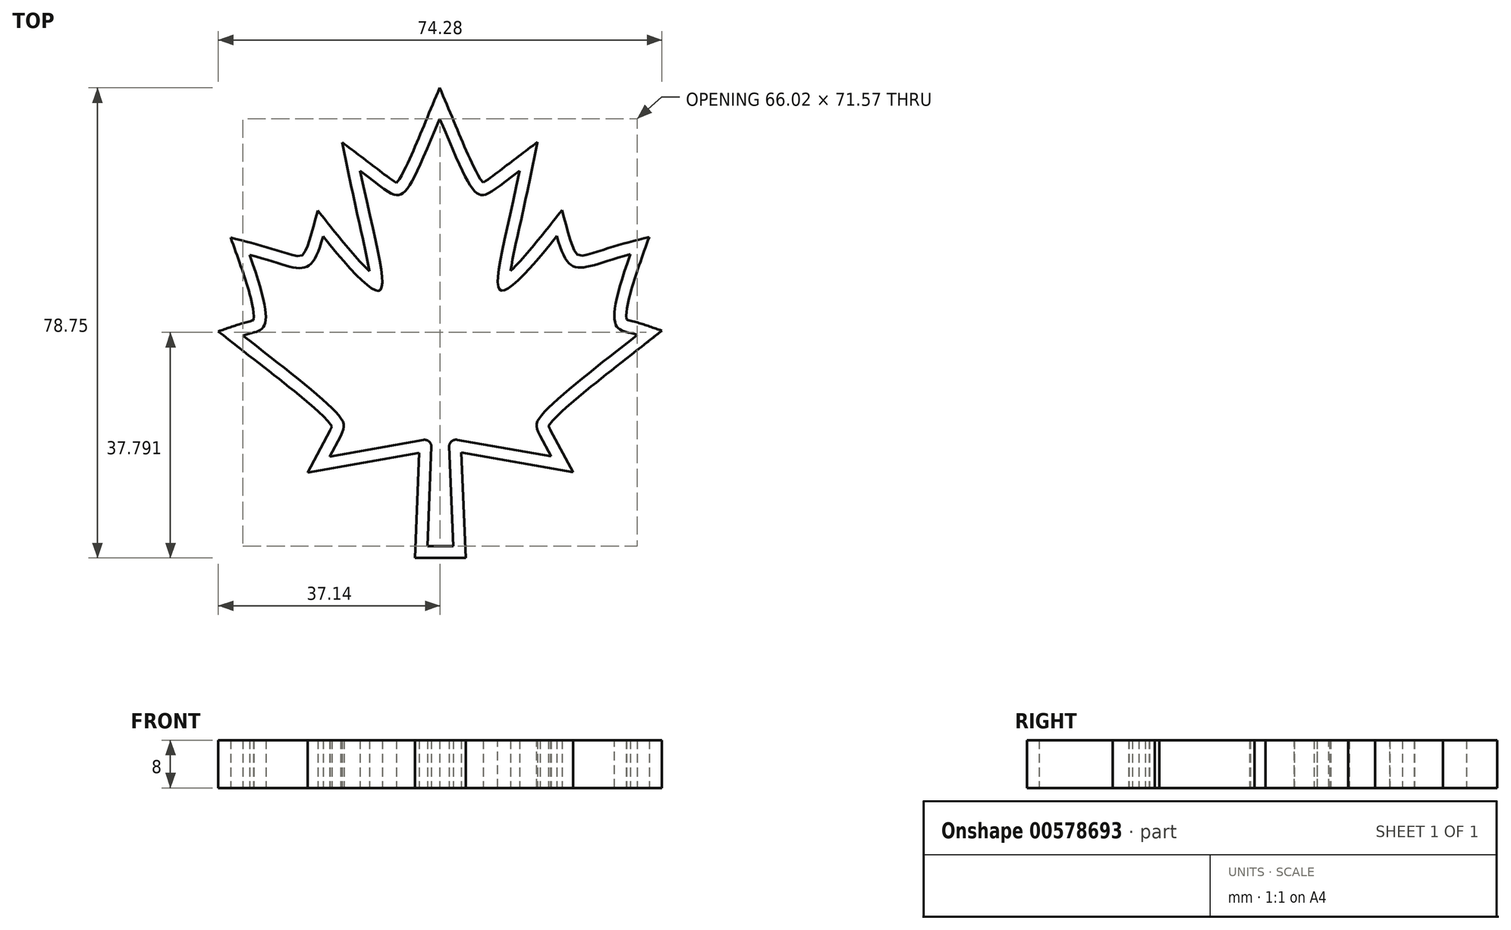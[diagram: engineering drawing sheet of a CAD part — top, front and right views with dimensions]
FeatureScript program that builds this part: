
annotation { "Feature Type Name" : "Feature", "Feature Type Description" : "" }
export const myFeature = defineFeature(function(context is Context, id is Id, definition is map)
    precondition{}
    {
        {
            var Q0;
            Q0=qCreatedBy(makeId("Top.planeOp"),FACE);
            var sketch = newSketch(context, id + "F0", { "sketchPlane" : qUnion([Q0])});
            skLineSegment(sketch, "E0", {"start": v(9.47, -7.07) * mm, "end": v(9.02, 3.36) * mm});
            skLineSegment(sketch, "E1", {"start": v(9.88, 4.04) * mm, "end": v(19.68, 2.32) * mm});
            skLineSegment(sketch, "E2", {"start": v(19.68, 2.32) * mm, "end": v(18.53, 4.47) * mm});
            skFitSpline(sketch, "E3", {"points": [v(18.53, 4.47) * mm, v(18.53, 6.4) * mm, v(28.7, 15.02) * mm], "startDerivative": vector(-4.89, 9.38) * mm, "endDerivative": vector(15.45, 12.25) * mm});
            skArc(sketch, "E4", {"start": v(9.88, 4.04) * mm, "mid": v(9.3, 3.9) * mm, "end": v(9.02, 3.36) * mm});
            skFitSpline(sketch, "E5", {"points": [v(28.7, 15.02) * mm, v(26.74, 15.72) * mm, v(28, 23.47) * mm], "startDerivative": vector(-7.73, 2.6) * mm, "endDerivative": vector(8.14, 22.87) * mm});
            skFitSpline(sketch, "E6", {"points": [v(28, 23.47) * mm, v(20.29, 25.37) * mm], "startDerivative": vector(-15.91, -4.18) * mm, "endDerivative": vector(-4.05, 14.65) * mm});
            skFitSpline(sketch, "E7", {"points": [v(20.29, 25.37) * mm, v(14.46, 19.67) * mm, v(16.38, 32.21) * mm], "startDerivative": vector(-16.61, -21.02) * mm, "endDerivative": vector(7.72, 38.13) * mm});
            skFitSpline(sketch, "E8", {"points": [v(16.38, 32.21) * mm, v(12.19, 29.72) * mm, v(8.04, 37.65) * mm], "startDerivative": vector(-19.33, -14.7) * mm, "endDerivative": vector(-11.74, 27.86) * mm});
            skLineSegment(sketch, "E9", {"start": v(9.47, -7.07) * mm, "end": v(8.11, -7.07) * mm});
            skFitSpline(sketch, "E10.MirrorCS", {"points": [v(-0.3, 32.18) * mm, v(3.91, 29.7) * mm, v(8.04, 37.65) * mm], "startDerivative": vector(19.38, -14.63) * mm, "endDerivative": vector(11.64, 27.9) * mm});
            skFitSpline(sketch, "E11.MirrorCS", {"points": [v(-4.17, 25.33) * mm, v(1.68, 19.65) * mm, v(-0.3, 32.18) * mm], "startDerivative": vector(16.68, -20.97) * mm, "endDerivative": vector(-7.85, 38.1) * mm});
            skFitSpline(sketch, "E12.MirrorCS", {"points": [v(-11.87, 23.4) * mm, v(-4.17, 25.33) * mm], "startDerivative": vector(15.93, -4.13) * mm, "endDerivative": vector(4, 14.66) * mm});
            skFitSpline(sketch, "E13.MirrorCS", {"points": [v(-12.56, 14.95) * mm, v(-10.59, 15.65) * mm, v(-11.87, 23.4) * mm], "startDerivative": vector(7.72, 2.63) * mm, "endDerivative": vector(-8.22, 22.84) * mm});
            skFitSpline(sketch, "E14.MirrorCS", {"points": [v(-2.35, 4.43) * mm, v(-2.35, 6.36) * mm, v(-12.56, 14.95) * mm], "startDerivative": vector(4.86, 9.4) * mm, "endDerivative": vector(-15.49, 12.2) * mm});
            skLineSegment(sketch, "E15.MirrorCS", {"start": v(-3.49, 2.28) * mm, "end": v(-2.35, 4.43) * mm});
            skLineSegment(sketch, "E16.MirrorCS", {"start": v(6.3, 4.03) * mm, "end": v(-3.49, 2.28) * mm});
            skArc(sketch, "E17.MirrorCS", {"start": v(6.3, 4.03) * mm, "mid": v(6.89, 3.89) * mm, "end": v(7.17, 3.36) * mm});
            skLineSegment(sketch, "E18.MirrorCS", {"start": v(6.75, -7.08) * mm, "end": v(7.17, 3.36) * mm});
            skLineSegment(sketch, "E19.MirrorCS", {"start": v(6.75, -7.08) * mm, "end": v(8.11, -7.07) * mm});
            skSolve(sketch);
        }
        {
            var Q0;
            Q0 = qSketchRegion(id + "F0", true);
            extrude(context, id + "F1", {"entities" : qUnion([Q0]), "depth" : 5 * mm, "offsetDistance" : 25 * mm});
        }
        {
            var Q0;
            Q0=makeQuery(id+"F1.opExtrude","SWEPT_BODY",BODY,{"disambiguationData":[OSD([sQuery(id+"F0.wireOp",EDGE,"E0"),sQuery(id+"F0.wireOp",EDGE,"E1"),sQuery(id+"F0.wireOp",EDGE,"E2"),sQuery(id+"F0.wireOp",EDGE,"E3"),sQuery(id+"F0.wireOp",EDGE,"E4"),sQuery(id+"F0.wireOp",EDGE,"E5"),sQuery(id+"F0.wireOp",EDGE,"E6"),sQuery(id+"F0.wireOp",EDGE,"E7"),sQuery(id+"F0.wireOp",EDGE,"E8"),sQuery(id+"F0.wireOp",EDGE,"E9"),sQuery(id+"F0.wireOp",EDGE,"E10.MirrorCS"),sQuery(id+"F0.wireOp",EDGE,"E11.MirrorCS"),sQuery(id+"F0.wireOp",EDGE,"E12.MirrorCS"),sQuery(id+"F0.wireOp",EDGE,"E13.MirrorCS"),sQuery(id+"F0.wireOp",EDGE,"E14.MirrorCS"),sQuery(id+"F0.wireOp",EDGE,"E15.MirrorCS"),sQuery(id+"F0.wireOp",EDGE,"E16.MirrorCS"),sQuery(id+"F0.wireOp",EDGE,"E17.MirrorCS"),sQuery(id+"F0.wireOp",EDGE,"E18.MirrorCS"),sQuery(id+"F0.wireOp",EDGE,"E19.MirrorCS")])]});
            var Q1;
            Q1=qCreatedBy(makeId("Origin.pointOp"),VERTEX);
            transform(context, id + "F2", {"entities" : qUnion([Q0]), "transformType" : TransformType.SCALE_UNIFORMLY, "scale" : 1.6, "scalePoint" : qUnion([Q1]), "makeCopy" : false});
        }
        {
            var Q0;
            Q0=makeQuery(id+"F1.opExtrude","CAP_FACE",FACE,{"disambiguationData":[OSD([sQuery(id+"F0.wireOp",EDGE,"E0"),sQuery(id+"F0.wireOp",EDGE,"E1"),sQuery(id+"F0.wireOp",EDGE,"E2"),sQuery(id+"F0.wireOp",EDGE,"E3"),sQuery(id+"F0.wireOp",EDGE,"E4"),sQuery(id+"F0.wireOp",EDGE,"E5"),sQuery(id+"F0.wireOp",EDGE,"E6"),sQuery(id+"F0.wireOp",EDGE,"E7"),sQuery(id+"F0.wireOp",EDGE,"E8"),sQuery(id+"F0.wireOp",EDGE,"E9"),sQuery(id+"F0.wireOp",EDGE,"E10.MirrorCS"),sQuery(id+"F0.wireOp",EDGE,"E11.MirrorCS"),sQuery(id+"F0.wireOp",EDGE,"E12.MirrorCS"),sQuery(id+"F0.wireOp",EDGE,"E13.MirrorCS"),sQuery(id+"F0.wireOp",EDGE,"E14.MirrorCS"),sQuery(id+"F0.wireOp",EDGE,"E15.MirrorCS"),sQuery(id+"F0.wireOp",EDGE,"E16.MirrorCS"),sQuery(id+"F0.wireOp",EDGE,"E17.MirrorCS"),sQuery(id+"F0.wireOp",EDGE,"E18.MirrorCS"),sQuery(id+"F0.wireOp",EDGE,"E19.MirrorCS")])],"isStart":false});
            var Q1;
            Q1=makeQuery(id+"F1.opExtrude","CAP_FACE",FACE,{"disambiguationData":[OSD([sQuery(id+"F0.wireOp",EDGE,"E0"),sQuery(id+"F0.wireOp",EDGE,"E1"),sQuery(id+"F0.wireOp",EDGE,"E2"),sQuery(id+"F0.wireOp",EDGE,"E3"),sQuery(id+"F0.wireOp",EDGE,"E4"),sQuery(id+"F0.wireOp",EDGE,"E5"),sQuery(id+"F0.wireOp",EDGE,"E6"),sQuery(id+"F0.wireOp",EDGE,"E7"),sQuery(id+"F0.wireOp",EDGE,"E8"),sQuery(id+"F0.wireOp",EDGE,"E9"),sQuery(id+"F0.wireOp",EDGE,"E10.MirrorCS"),sQuery(id+"F0.wireOp",EDGE,"E11.MirrorCS"),sQuery(id+"F0.wireOp",EDGE,"E12.MirrorCS"),sQuery(id+"F0.wireOp",EDGE,"E13.MirrorCS"),sQuery(id+"F0.wireOp",EDGE,"E14.MirrorCS"),sQuery(id+"F0.wireOp",EDGE,"E15.MirrorCS"),sQuery(id+"F0.wireOp",EDGE,"E16.MirrorCS"),sQuery(id+"F0.wireOp",EDGE,"E17.MirrorCS"),sQuery(id+"F0.wireOp",EDGE,"E18.MirrorCS"),sQuery(id+"F0.wireOp",EDGE,"E19.MirrorCS")])],"isStart":true});
            shell(context, id + "F3", {"entities" : qUnion([Q0, Q1]), "thickness" : 2 * mm, "oppositeDirection" : true});
        }
    });
